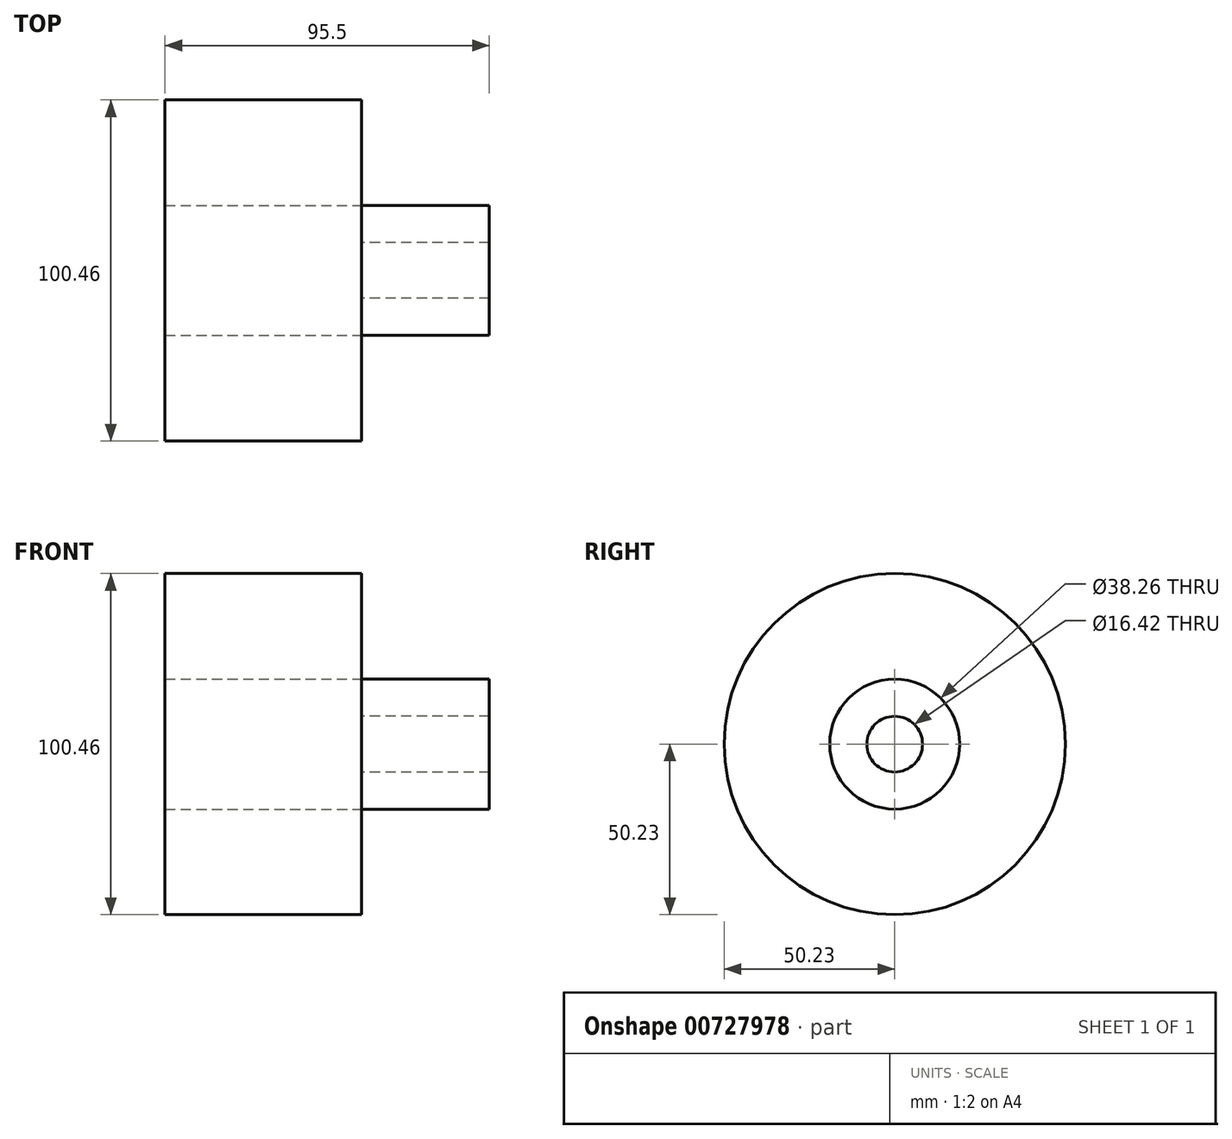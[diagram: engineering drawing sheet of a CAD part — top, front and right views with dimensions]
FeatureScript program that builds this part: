
annotation { "Feature Type Name" : "Feature", "Feature Type Description" : "" }
export const myFeature = defineFeature(function(context is Context, id is Id, definition is map)
    precondition{}
    {
        {
            var Q0;
            Q0=qCreatedBy(makeId("Right.planeOp"),FACE);
            var sketch = newSketch(context, id + "F0", { "sketchPlane" : qUnion([Q0])});
            skCircle(sketch, "E0", {"center": v(0, 0) * mm, "radius": 19.13 * mm});
            skCircle(sketch, "E1", {"center": v(0, 0) * mm, "radius": 27.27 * mm});
            skCircle(sketch, "E2", {"center": v(0, 0) * mm, "radius": 50.23 * mm});
            skCircle(sketch, "E3", {"center": v(0, 0) * mm, "radius": 8.21 * mm});
            skSolve(sketch);
        }
        {
            var Q0;
            Q0=makeQuery(id+"F0.imprint","IMPRINT",FACE,{"disambiguationData":[TD([[makeQuery(id+"F0.imprint","IMPRINT",EDGE,{"derivedFrom":sQuery(id+"F0.wireOp",EDGE,"E0")}),1.0]])]});
            extrude(context, id + "F1", {"entities" : qUnion([Q0]), "depth" : 37.6 * mm, "offsetDistance" : 25.4 * mm});
        }
        {
            var Q0;
            Q0=makeQuery(id+"F0.imprint","IMPRINT",FACE,{"disambiguationData":[TD([[makeQuery(id+"F0.imprint","IMPRINT",EDGE,{"derivedFrom":sQuery(id+"F0.wireOp",EDGE,"E1")}),-1.0]])]});
            var Q1;
            Q1=makeQuery(id+"F0.imprint","IMPRINT",FACE,{"disambiguationData":[TD([[makeQuery(id+"F0.imprint","IMPRINT",EDGE,{"derivedFrom":sQuery(id+"F0.wireOp",EDGE,"E0")}),-1.0]])]});
            extrude(context, id + "F2", {"entities" : qUnion([Q0, Q1]), "oppositeDirection" : true, "depth" : 57.9 * mm, "offsetDistance" : 25.4 * mm});
        }
        {
            var Q0;
            Q0=makeQuery(id+"F0.imprint","IMPRINT",FACE,{"disambiguationData":[TD([[makeQuery(id+"F0.imprint","IMPRINT",EDGE,{"derivedFrom":sQuery(id+"F0.wireOp",EDGE,"E3")}),1.0]])]});
            extrude(context, id + "F3", {"entities" : qUnion([Q0]), "operationType" : NewBodyOperationType.REMOVE, "endBound" : BoundingType.THROUGH_ALL, "oppositeDirection" : true, "depth" : 25.4 * mm, "offsetDistance" : 25.4 * mm});
        }
    });
